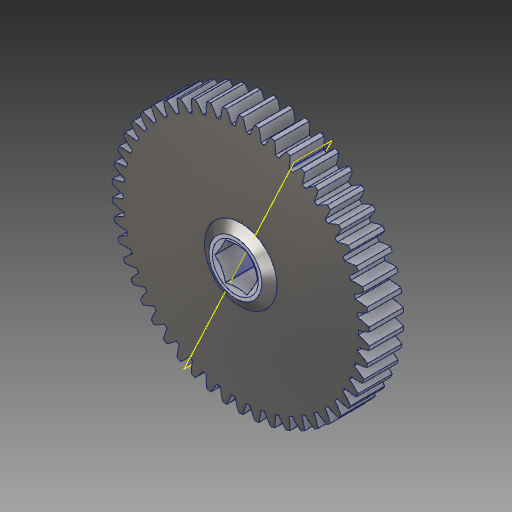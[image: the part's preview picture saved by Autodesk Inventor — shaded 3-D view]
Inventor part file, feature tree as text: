
AUTODESK INVENTOR PART (.ipt)
format: ipt  version: 2017.1 (Build 211199000, 199)  size: 474,624 bytes
history: native  units: in
note: dims shown in document units (in); Inventor stores cm internally (conversion verified against a paired STEP export)
features: plane x1, imported_body x1
ambient origin geometry x8: Origin, YZ Plane, XZ Plane, XY Plane, X Axis, Y Axis, Z Axis, Center Point
bodies: Solid1 (feature_tree)
feature tree (2):
  plane  "Work Plane2"
  imported_body  "Imported1"
